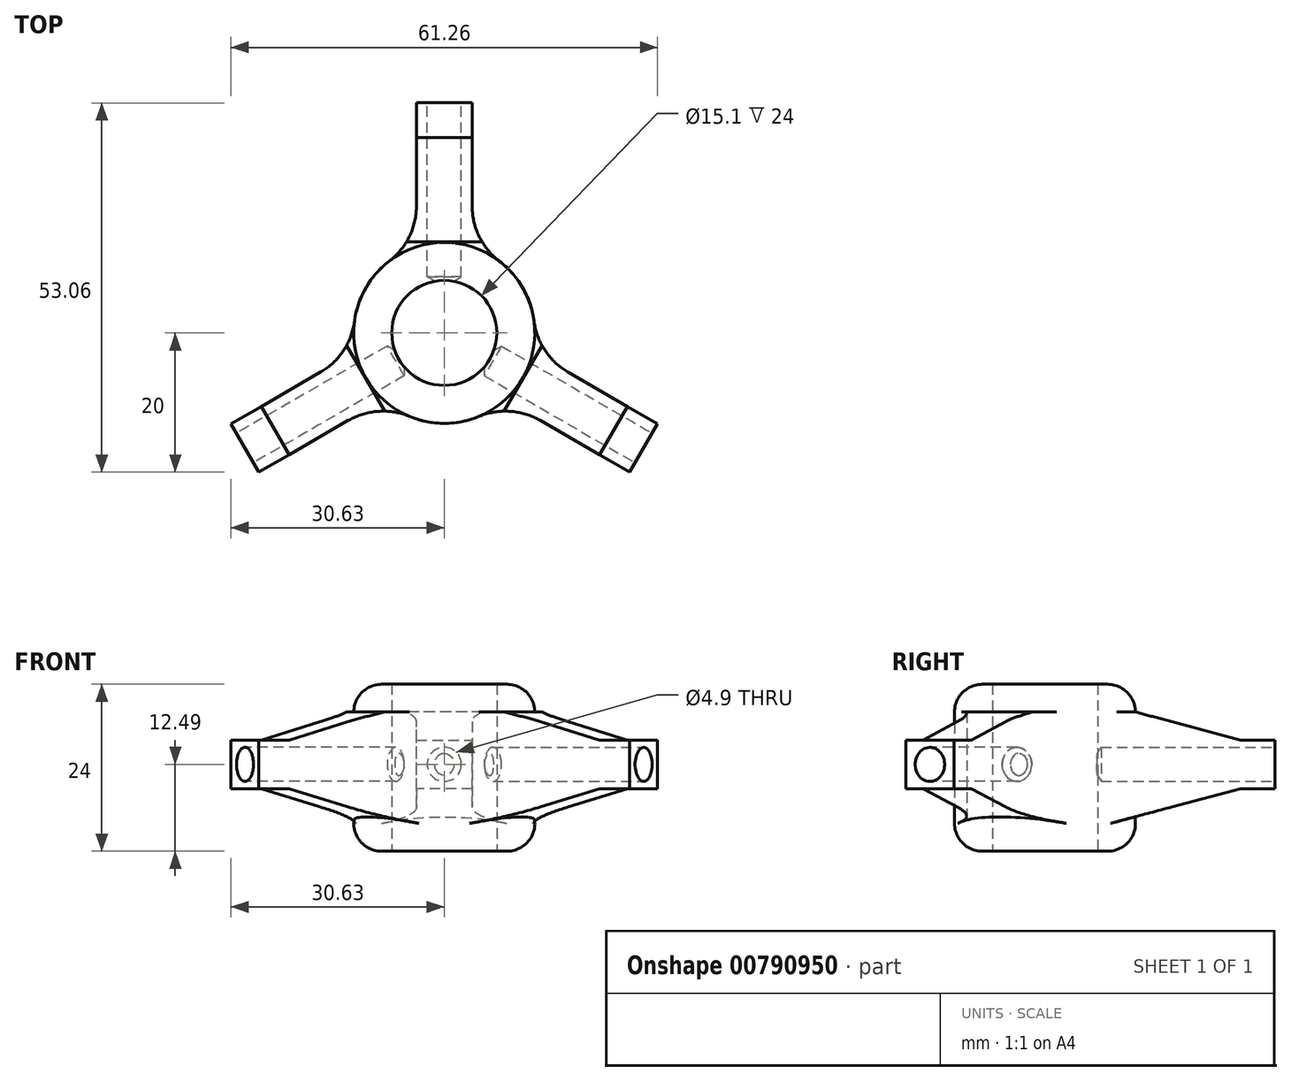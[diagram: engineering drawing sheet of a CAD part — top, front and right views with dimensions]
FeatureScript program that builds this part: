
annotation { "Feature Type Name" : "Feature", "Feature Type Description" : "" }
export const myFeature = defineFeature(function(context is Context, id is Id, definition is map)
    precondition{}
    {
        {
            var Q0;
            Q0=qCreatedBy(makeId("Top.planeOp"),FACE);
            var sketch = newSketch(context, id + "F0", { "sketchPlane" : qUnion([Q0])});
            skCircle(sketch, "E0", {"center": v(0, 0) * mm, "radius": 13 * mm});
            skCircle(sketch, "E1", {"center": v(0, 0) * mm, "radius": 7.55 * mm});
            skSolve(sketch);
        }
        {
            var Q0;
            Q0=makeQuery(id+"F0.imprint","IMPRINT",FACE,{"disambiguationData":[TD([[makeQuery(id+"F0.imprint","IMPRINT",EDGE,{"derivedFrom":sQuery(id+"F0.wireOp",EDGE,"E0")}),1.0]])]});
            extrude(context, id + "F1", {"entities" : qUnion([Q0]), "depth" : 24 * mm, "offsetDistance" : 25 * mm});
        }
        {
            var Q0;
            Q0=makeQuery(id+"F1.opExtrude","CAP_EDGE",EDGE,{"disambiguationData":[OSD([sQuery(id+"F0.wireOp",EDGE,"E0")])],"isStart":false});
            var Q1;
            Q1=makeQuery(id+"F1.opExtrude","CAP_EDGE",EDGE,{"disambiguationData":[OSD([sQuery(id+"F0.wireOp",EDGE,"E0")])],"isStart":true});
            fillet(context, id + "F2", {"entities" : qUnion([Q0, Q1]), "radius" : 4 * mm, "tangentPropagation" : true, "allowEdgeOverflow" : false});
        }
        {
            var Q0;
            Q0=makeQuery(id+"F1.opExtrude","CAP_FACE",FACE,{"disambiguationData":[OSD([sQuery(id+"F0.wireOp",EDGE,"E0"),sQuery(id+"F0.wireOp",EDGE,"E1")])],"isStart":false});
            var sketch = newSketch(context, id + "F3", { "sketchPlane" : qUnion([Q0])});
            skLineSegment(sketch, "E2.bottom", {"start": v(4, 8.06) * mm, "end": v(-4, 8.06) * mm});
            skLineSegment(sketch, "E2.top", {"start": v(4, 28.06) * mm, "end": v(-4, 28.06) * mm});
            skLineSegment(sketch, "E2.left", {"start": v(4, 8.06) * mm, "end": v(4, 28.06) * mm});
            skLineSegment(sketch, "E2.right", {"start": v(-4, 8.06) * mm, "end": v(-4, 28.06) * mm});
            skPoint(sketch, "E2.middle", {"position": v(0, 18.06) * mm});
            skLineSegment(sketch, "E3.1.0", {"start": v(-4.98, -7.5) * mm, "end": v(-22.3, -17.5) * mm});
            skLineSegment(sketch, "E3.1.1", {"start": v(-8.98, -0.57) * mm, "end": v(-4.98, -7.5) * mm});
            skLineSegment(sketch, "E3.1.2", {"start": v(-8.98, -0.57) * mm, "end": v(-26.3, -10.57) * mm});
            skLineSegment(sketch, "E3.1.3", {"start": v(-26.3, -10.57) * mm, "end": v(-22.3, -17.5) * mm});
            skLineSegment(sketch, "E3.2.0", {"start": v(8.98, -0.57) * mm, "end": v(26.3, -10.57) * mm});
            skLineSegment(sketch, "E3.2.1", {"start": v(4.98, -7.5) * mm, "end": v(8.98, -0.57) * mm});
            skLineSegment(sketch, "E3.2.2", {"start": v(4.98, -7.5) * mm, "end": v(22.3, -17.5) * mm});
            skLineSegment(sketch, "E3.2.3", {"start": v(22.3, -17.5) * mm, "end": v(26.3, -10.57) * mm});
            skPoint(sketch, "E3.center", {"position": v(0, 0) * mm});
            skSolve(sketch);
        }
        {
            var Q0;
            Q0=makeQuery(id+"F3.imprint","IMPRINT",FACE,{"disambiguationData":[TD([[makeQuery(id+"F3.imprint","IMPRINT",EDGE,{"derivedFrom":sQuery(id+"F3.wireOp",EDGE,"E2.top")}),1.0]])]});
            var Q1;
            {var subQ0=sQuery(id+"F3.wireOp",EDGE,"E3.1.0");Q1=makeQuery(id+"F3.imprint","IMPRINT",FACE,{"disambiguationData":[TD([[makeQuery(id+"F3.imprint","IMPRINT",EDGE,{"derivedFrom":subQ0}),-1.0]])]});}
            var Q2;
            {var subQ0=sQuery(id+"F3.wireOp",EDGE,"E3.2.0");Q2=makeQuery(id+"F3.imprint","IMPRINT",FACE,{"disambiguationData":[TD([[makeQuery(id+"F3.imprint","IMPRINT",EDGE,{"derivedFrom":subQ0}),-1.0]])]});}
            extrude(context, id + "F4", {"entities" : qUnion([Q0, Q1, Q2]), "operationType" : NewBodyOperationType.ADD, "oppositeDirection" : true, "depth" : 20 * mm, "offsetDistance" : 25 * mm, "hasSecondDirection" : true, "secondDirectionOppositeDirection" : true, "secondDirectionDepth" : 4 * mm});
        }
        {
            var Q0;
            Q0=makeQuery(id+"F4.boolean.opBoolean","INTERSECT",EDGE,{"derivedFrom":[makeQuery(id+"F1.opExtrude","SWEPT_FACE",FACE,{"disambiguationData":[OSD([sQuery(id+"F0.wireOp",EDGE,"E0")])]}),makeQuery(id+"F4.opExtrude","SWEPT_FACE",FACE,{"disambiguationData":[OSD([sQuery(id+"F3.wireOp",EDGE,"E3.1.0")])]})]});
            var Q1;
            Q1=makeQuery(id+"F4.boolean.opBoolean","INTERSECT",EDGE,{"derivedFrom":[makeQuery(id+"F1.opExtrude","SWEPT_FACE",FACE,{"disambiguationData":[OSD([sQuery(id+"F0.wireOp",EDGE,"E0")])]}),makeQuery(id+"F4.opExtrude","SWEPT_FACE",FACE,{"disambiguationData":[OSD([sQuery(id+"F3.wireOp",EDGE,"E3.1.2")])]})]});
            var Q2;
            Q2=makeQuery(id+"F4.boolean.opBoolean","INTERSECT",EDGE,{"derivedFrom":[makeQuery(id+"F1.opExtrude","SWEPT_FACE",FACE,{"disambiguationData":[OSD([sQuery(id+"F0.wireOp",EDGE,"E0")])]}),makeQuery(id+"F4.opExtrude","SWEPT_FACE",FACE,{"disambiguationData":[OSD([sQuery(id+"F3.wireOp",EDGE,"E2.right")])]})]});
            var Q3;
            Q3=makeQuery(id+"F4.boolean.opBoolean","INTERSECT",EDGE,{"derivedFrom":[makeQuery(id+"F1.opExtrude","SWEPT_FACE",FACE,{"disambiguationData":[OSD([sQuery(id+"F0.wireOp",EDGE,"E0")])]}),makeQuery(id+"F4.opExtrude","SWEPT_FACE",FACE,{"disambiguationData":[OSD([sQuery(id+"F3.wireOp",EDGE,"E2.left")])]})]});
            var Q4;
            Q4=makeQuery(id+"F4.boolean.opBoolean","INTERSECT",EDGE,{"derivedFrom":[makeQuery(id+"F1.opExtrude","SWEPT_FACE",FACE,{"disambiguationData":[OSD([sQuery(id+"F0.wireOp",EDGE,"E0")])]}),makeQuery(id+"F4.opExtrude","SWEPT_FACE",FACE,{"disambiguationData":[OSD([sQuery(id+"F3.wireOp",EDGE,"E3.2.0")])]})]});
            var Q5;
            Q5=makeQuery(id+"F4.boolean.opBoolean","INTERSECT",EDGE,{"derivedFrom":[makeQuery(id+"F1.opExtrude","SWEPT_FACE",FACE,{"disambiguationData":[OSD([sQuery(id+"F0.wireOp",EDGE,"E0")])]}),makeQuery(id+"F4.opExtrude","SWEPT_FACE",FACE,{"disambiguationData":[OSD([sQuery(id+"F3.wireOp",EDGE,"E3.2.2")])]})]});
            fillet(context, id + "F5", {"entities" : qUnion([Q0, Q1, Q2, Q3, Q4, Q5]), "radius" : 10 * mm, "tangentPropagation" : true, "allowEdgeOverflow" : false});
        }
        {
            var Q0;
            Q0=makeQuery(id+"F4.opExtrude","CAP_EDGE",EDGE,{"disambiguationData":[OSD([sQuery(id+"F3.wireOp",EDGE,"E3.1.3")])],"isStart":true});
            var Q1;
            Q1=makeQuery(id+"F4.opExtrude","CAP_EDGE",EDGE,{"disambiguationData":[OSD([sQuery(id+"F3.wireOp",EDGE,"E3.2.3")])],"isStart":true});
            var Q2;
            Q2=makeQuery(id+"F4.opExtrude","CAP_EDGE",EDGE,{"disambiguationData":[OSD([sQuery(id+"F3.wireOp",EDGE,"E2.top")])],"isStart":true});
            chamfer(context, id + "F6", {"entities" : qUnion([Q0, Q1, Q2]), "chamferType" : ChamferType.OFFSET_ANGLE, "width" : 15 * mm, "oppositeDirection" : false, "angle" : 15 * degree, "tangentPropagation" : true});
        }
        {
            var Q0;
            Q0=makeQuery(id+"F4.opExtrude","CAP_EDGE",EDGE,{"disambiguationData":[OSD([sQuery(id+"F3.wireOp",EDGE,"E3.2.3")])],"isStart":false});
            var Q1;
            {var subQ0=sQuery(id+"F3.wireOp",EDGE,"E3.1.3");Q1=makeQuery(id+"F6.opChamfer","BLEND_EDGE",EDGE,{"blendedFrom":[makeQuery(id+"F4.opExtrude","CAP_EDGE",EDGE,{"disambiguationData":[OSD([subQ0])],"isStart":false}),makeQuery(id+"F4.opExtrude","SWEPT_FACE",FACE,{"disambiguationData":[OSD([subQ0])]})],"blendedInto":[makeQuery(id+"F4.opExtrude","SWEPT_FACE",FACE,{"disambiguationData":[OSD([subQ0])]})]});}
            var Q2;
            Q2=makeQuery(id+"F4.opExtrude","CAP_EDGE",EDGE,{"disambiguationData":[OSD([sQuery(id+"F3.wireOp",EDGE,"E2.top")])],"isStart":false});
            var Q3;
            Q3=makeQuery(id+"F4.opExtrude","CAP_EDGE",EDGE,{"disambiguationData":[OSD([sQuery(id+"F3.wireOp",EDGE,"E3.1.3")])],"isStart":false});
            chamfer(context, id + "F7", {"entities" : qUnion([Q0, Q1, Q2, Q3]), "chamferType" : ChamferType.OFFSET_ANGLE, "width" : 5 * mm, "oppositeDirection" : false, "angle" : 75 * degree, "tangentPropagation" : true});
        }
        {
            var Q0;
            Q0=makeQuery(id+"F4.opExtrude","SWEPT_FACE",FACE,{"disambiguationData":[OSD([sQuery(id+"F3.wireOp",EDGE,"E3.1.3")])]});
            extrude(context, id + "F8", {"entities" : qUnion([Q0]), "operationType" : NewBodyOperationType.ADD, "depth" : 5 * mm, "offsetDistance" : 25 * mm});
        }
        {
            var Q0;
            Q0=makeQuery(id+"F4.opExtrude","SWEPT_FACE",FACE,{"disambiguationData":[OSD([sQuery(id+"F3.wireOp",EDGE,"E3.2.3")])]});
            extrude(context, id + "F9", {"entities" : qUnion([Q0]), "operationType" : NewBodyOperationType.ADD, "depth" : 5 * mm, "offsetDistance" : 25 * mm});
        }
        {
            var Q0;
            Q0=makeQuery(id+"F4.opExtrude","SWEPT_FACE",FACE,{"disambiguationData":[OSD([sQuery(id+"F3.wireOp",EDGE,"E2.top")])]});
            extrude(context, id + "F10", {"entities" : qUnion([Q0]), "operationType" : NewBodyOperationType.ADD, "depth" : 5 * mm, "offsetDistance" : 25 * mm});
        }
        {
            var Q0;
            Q0=makeQuery(id+"F9.opExtrude","CAP_FACE",FACE,{"disambiguationData":[OSD([sQuery(id+"F3.wireOp",EDGE,"E3.2.3")])],"isStart":false});
            var sketch = newSketch(context, id + "F11", { "sketchPlane" : qUnion([Q0])});
            skPoint(sketch, "E4", {"position": v(0, 12.48) * mm});
            skSolve(sketch);
        }
        {
            var Q0;
            Q0=sQuery(id+"F11.wireOp",VERTEX,"E4");
            var Q1;
            Q1=makeQuery(id+"F1.opExtrude","SWEPT_BODY",BODY,{"disambiguationData":[OSD([sQuery(id+"F0.wireOp",EDGE,"E0"),sQuery(id+"F0.wireOp",EDGE,"E1")])]});
            hole(context, id + "F12", {"style" : HoleStyle.SIMPLE, "endStyle" : HoleEndStyle.BLIND, "holeDiameter" : 4.9 * mm, "majorDiameter" : 5 * mm, "holeDepth" : 25 * mm, "isTappedThrough" : true, "tappedDepth" : 5 * mm, "tapClearance" : 3, "startFromSketch" : true, "locations" : qUnion([Q0]), "scope" : qUnion([Q1])});
        }
        {
            var Q0;
            Q0=makeQuery(id+"F10.opExtrude","CAP_FACE",FACE,{"disambiguationData":[OSD([sQuery(id+"F3.wireOp",EDGE,"E2.top")])],"isStart":false});
            var sketch = newSketch(context, id + "F13", { "sketchPlane" : qUnion([Q0])});
            skPoint(sketch, "E5", {"position": v(0, 12.5) * mm});
            skPoint(sketch, "E5.positionSnap0", {"position": v(-4, 12.5) * mm});
            skSolve(sketch);
        }
        {
            var Q0;
            Q0=sQuery(id+"F13.wireOp",VERTEX,"E5");
            var Q1;
            Q1=makeQuery(id+"F1.opExtrude","SWEPT_BODY",BODY,{"disambiguationData":[OSD([sQuery(id+"F0.wireOp",EDGE,"E0"),sQuery(id+"F0.wireOp",EDGE,"E1")])]});
            hole(context, id + "F14", {"style" : HoleStyle.SIMPLE, "endStyle" : HoleEndStyle.BLIND, "holeDiameter" : 4.9 * mm, "majorDiameter" : 5 * mm, "holeDepth" : 25 * mm, "isTappedThrough" : true, "tappedDepth" : 5 * mm, "tapClearance" : 3, "startFromSketch" : true, "locations" : qUnion([Q0]), "scope" : qUnion([Q1])});
        }
        {
            var Q0;
            Q0=makeQuery(id+"F8.opExtrude","CAP_FACE",FACE,{"disambiguationData":[OSD([sQuery(id+"F3.wireOp",EDGE,"E3.1.3")])],"isStart":false});
            var sketch = newSketch(context, id + "F15", { "sketchPlane" : qUnion([Q0])});
            skPoint(sketch, "E6", {"position": v(0, 12.5) * mm});
            skPoint(sketch, "E6.positionSnap0", {"position": v(0, 8.6) * mm});
            skPoint(sketch, "E6.positionSnap1", {"position": v(-4, 12.5) * mm});
            skSolve(sketch);
        }
        {
            var Q0;
            Q0=sQuery(id+"F15.wireOp",VERTEX,"E6");
            var Q1;
            Q1=makeQuery(id+"F1.opExtrude","SWEPT_BODY",BODY,{"disambiguationData":[OSD([sQuery(id+"F0.wireOp",EDGE,"E0"),sQuery(id+"F0.wireOp",EDGE,"E1")])]});
            hole(context, id + "F16", {"style" : HoleStyle.SIMPLE, "endStyle" : HoleEndStyle.BLIND, "holeDiameter" : 4.9 * mm, "majorDiameter" : 5 * mm, "holeDepth" : 25 * mm, "isTappedThrough" : true, "tappedDepth" : 5 * mm, "tapClearance" : 3, "startFromSketch" : true, "locations" : qUnion([Q0]), "scope" : qUnion([Q1])});
        }
    });
